# Revit family: RoofCap_Westlake-Royal-Roofing_HighProfileConcreteTiles
name_source: partatom
category: Generic Models
units: mm (PartAtom-declared; Revit-internal decimal feet)

## family parameters
Can host rebar = No
Classification Number = 23.35.20.11.14
Cut with Voids When Loaded = No
Maintain Annotation Orientation = No
Part Type = Normal
Room Calculation Point = No
Round Connector Dimension = Use Diameter
Shared = No

## types (1)
- Type as Specified in 07 32 16
    Assembly Code = B3010150
    Cap Exposure = 1' - 0"
    Cost = 0 $
    Default Elevation = 0' - 0"
    Description = Concrete Tile Cap As Specified in 07 32 16
    Green Building-LEED = https://www.arcat.com
    Installation Phase = Exterior Roof Finishes
    Keynote = 07 32 16
    Maintenance Schedule (Months) = 12
    Manufacturer = Westlake Royal Roofing Solutions
    Material = Boral_Material-as-Specified
    Model = As Specified in 07 32 16
    Product Data = https://www.arcat.com
    Specification = https://www.arcat.com
    URL = https://westlakeroyalroofing.com
    Warranty Duration (Years) = 3

## geometry (parser evidence)
native form markers: Blend x6, Sweep x5
no freeform markers — native parametric forms only
